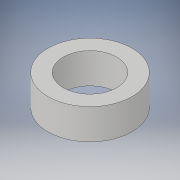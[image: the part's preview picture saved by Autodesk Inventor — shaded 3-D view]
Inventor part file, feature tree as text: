
AUTODESK INVENTOR PART (.ipt)
format: ipt  version: 2018 (Build 220112000, 112)  size: 96,256 bytes
history: native  units: in
note: dims shown in document units (in); Inventor stores cm internally (conversion verified against a paired STEP export)
features: extrude x1, sketch x1
ambient origin geometry x8: Origin, YZ Plane, XZ Plane, XY Plane, X Axis, Y Axis, Z Axis, Center Point
bodies: Solid1 (feature_tree)
feature tree (2):
  extrude  "Extrusion1"  Depth=0.0787in
  sketch  "Sketch1"  dims[d0=0.1378in d1=0.2165in d2=0.0787in d3=0.0in]
